# Revit family: SHP Pump (Single Speed)
name_source: partatom
category: Mechanical Equipment
units: mm (PartAtom-declared; Revit-internal decimal feet)

## family parameters
Always vertical = Yes
Classification = Pump
Cut with Voids When Loaded = No
OmniClass Number = 23.60.30.21
OmniClass Title = Pumps
Part Type = Normal
Room Calculation Point = No
Round Connector Dimension = Use Radius
Shared = No
Work Plane-Based = No

## types (8) — shared parameters
Anchor Points (Center to Center) = 9"
Assembly Code = D2090400
Black = Fluidra Base
Description = Jandy Commercial Stealth Pump DOE Compliant
Fluidra_Apparent_Load = 0 VA
Fluidra_Cos ϕ = 100.00%
Fluidra_Description = Jandy Commercial Stealth Pump DOE Compliant
Fluidra_Frequency = 60 Hz
Fluidra_Manufacturer = Fluidra
Fluidra_Voltage = 208 V
Front to Anchor Points (Center) = 11 5/8"
Front to Outlet (Center) = 14"
Inlet Height (Center) = 10 3/8"
Lid = Fluidra Lid
Manufacturer = Fluidra
Pump Height = 15 1/4"
Pump Width (Lid Tabs) = 12 15/16"
URL = https://www.jandy.com
Union Diameter = 2"

## per-type parameters (varying)
| type | 5HP 3PH Components | Fluidra_Amps_(115V) | Fluidra_Amps_(208V) | Fluidra_Amps_(230V) | Fluidra_Amps_(460V) | Fluidra_Phase | Fluidra_Recommended_Pipe_Size | Fluidra_THP | Fluidra_Union_Size | Fluidra_Voltage (High) | Fluidra_Voltage (Low) | Fluidra_WEF | Fluidra_Weight | Pump Length | Single Phase Capacitor |
| SHPF.50 | No | 9 A | 5 A | 4 A | 0 A | 1 | 2" - 2.5" | 1 hp | 2" - 2.5" | 230 V | 115 V | 3.6 | 30.00 lb | 29" | Yes |
| SHPM.75 | No | 9 A | 5 A | 4 A | 0 A | 1 | 2" - 2.5" | 1 hp | 2" - 2.5" | 230 V | 115 V | 3.6 | 30.00 lb | 29" | Yes |
| SHPF5.0 | No | 0 A | 21 A | 19 A | 0 A | 1 | 4" | 5 hp | 2.5" - 3" | 230 V | 0 V |  | 68.00 lb | 31 1/2" | Yes |
| SHPF1.0-3PH | No | 0 A | 5 A | 5 A | 2 A | 3 | 2" - 2.5" | 2 hp | 2" - 2.5" | 460 V | 230 V | 2.7 | 55.00 lb | 29 3/4" | No |
| SHPF1.5-3PH | No | 0 A | 6 A | 6 A | 3 A | 3 | 2" - 2.5" | 2 hp | 2" - 2.5" | 460 V | 230 V | 2.6 | 57.00 lb | 30" | No |
| SHPF2.0-3PH | No | 0 A | 7 A | 7 A | 3 A | 3 | 2" - 2.5" | 3 hp | 2" - 2.5" | 460 V | 230 V | 2.5 | 64.00 lb | 30 1/2" | No |
| SHPF3.0-3PH | No | 0 A | 9 A | 9 A | 4 A | 3 | 2.5" - 3" | 3 hp | 2" - 2.5" | 460 V | 230 V | 2.1 | 62.00 lb | 31 1/2" | No |
| SHPF5.0-3PH | Yes | 0 A | 16 A | 15 A | 8 A | 3 | 4" | 6 hp | 2.5" - 3" | 460 V | 230 V | 1.8 | 95.00 lb | 35" | No |

note: column(s) folded — value = type name in every type: Fluidra_Model, Model

## geometry (parser evidence)
native form markers: Sweep x10
no freeform markers — native parametric forms only
